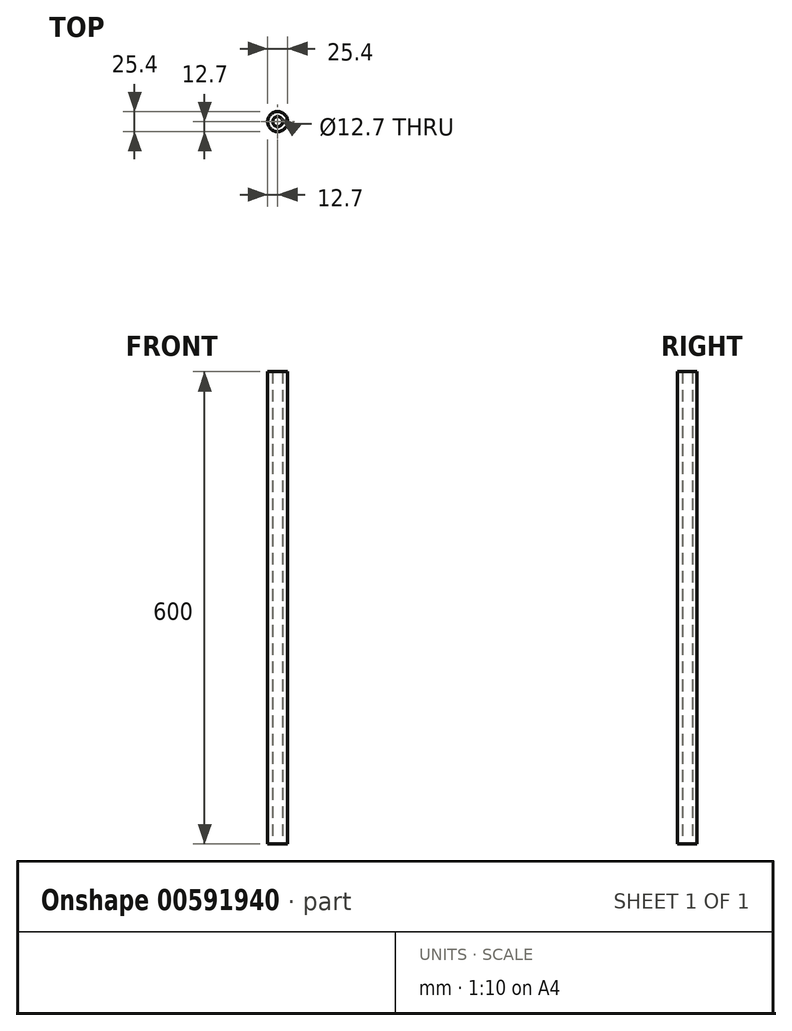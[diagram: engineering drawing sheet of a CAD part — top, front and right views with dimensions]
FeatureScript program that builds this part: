
annotation { "Feature Type Name" : "Feature", "Feature Type Description" : "" }
export const myFeature = defineFeature(function(context is Context, id is Id, definition is map)
    precondition{}
    {
        {
            var Q0;
            Q0=qCreatedBy(makeId("Top.planeOp"),FACE);
            var sketch = newSketch(context, id + "F0", { "sketchPlane" : qUnion([Q0])});
            skCircle(sketch, "E0", {"center": v(0, 0) * mm, "radius": 12.7 * mm});
            skCircle(sketch, "E1", {"center": v(0, 0) * mm, "radius": 6.35 * mm});
            skSolve(sketch);
        }
        {
            var Q0;
            Q0=qSketchRegion(id+"F0",true);
            extrude(context, id + "F1", {"entities" : qUnion([Q0]), "depth" : 600 * mm, "offsetDistance" : 25.4 * mm});
        }
    });
